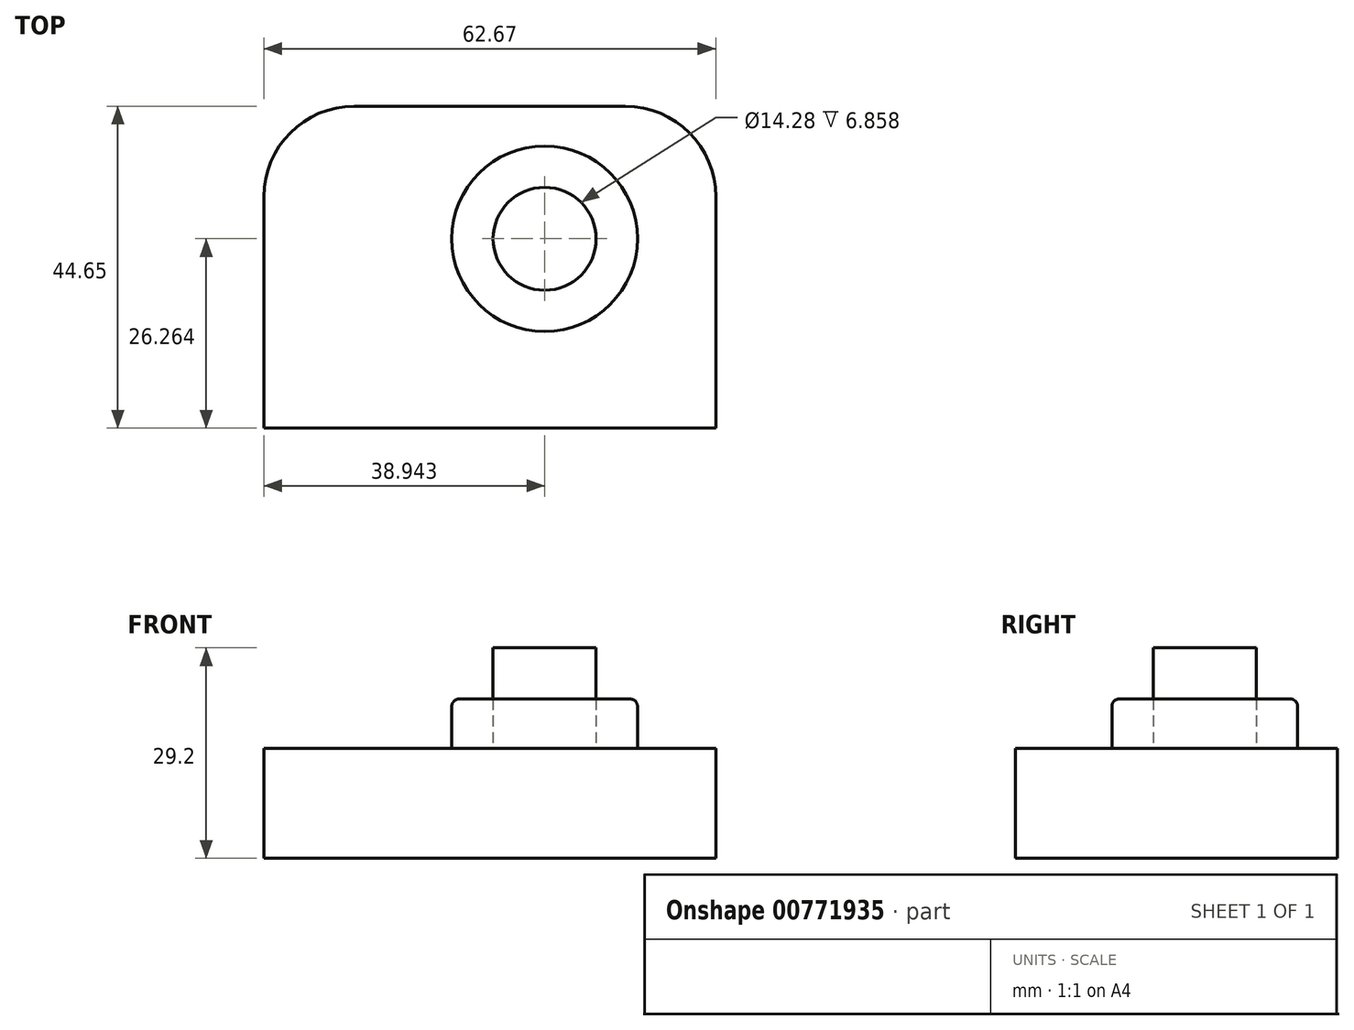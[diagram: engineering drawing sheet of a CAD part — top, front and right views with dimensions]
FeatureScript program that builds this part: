
annotation { "Feature Type Name" : "Feature", "Feature Type Description" : "" }
export const myFeature = defineFeature(function(context is Context, id is Id, definition is map)
    precondition{}
    {
        {
            var Q0;
            Q0=qCreatedBy(makeId("Top.planeOp"),FACE);
            var sketch = newSketch(context, id + "F0", { "sketchPlane" : qUnion([Q0])});
            skLineSegment(sketch, "E0.bottom", {"start": v(-68.94, 0) * mm, "end": v(-6.27, 0) * mm});
            skLineSegment(sketch, "E0.top", {"start": v(-68.94, -44.65) * mm, "end": v(-6.27, -44.65) * mm});
            skLineSegment(sketch, "E0.left", {"start": v(-68.94, 0) * mm, "end": v(-68.94, -44.65) * mm});
            skLineSegment(sketch, "E0.right", {"start": v(-6.27, 0) * mm, "end": v(-6.27, -44.65) * mm});
            skSolve(sketch);
        }
        {
            var Q0;
            Q0=qCreatedBy(makeId("Top.planeOp"),FACE);
            var sketch = newSketch(context, id + "F1", { "sketchPlane" : qUnion([Q0])});
            skSolve(sketch);
        }
        {
            var Q0;
            Q0 = qSketchRegion(id + "F1", true);
            var Q1;
            Q1=makeQuery(id+"F0.imprint","IMPRINT",FACE,{"disambiguationData":[TD([[makeQuery(id+"F0.imprint","IMPRINT",EDGE,{"derivedFrom":sQuery(id+"F0.wireOp",EDGE,"E0.bottom")}),-1.0]])]});
            extrude(context, id + "F2", {"entities" : qUnion([Q0, Q1]), "depth" : 15.24 * mm, "offsetDistance" : 25.4 * mm});
        }
        {
            var Q0;
            Q0=qCreatedBy(makeId("Top.planeOp"),FACE);
            var sketch = newSketch(context, id + "F3", { "sketchPlane" : qUnion([Q0])});
            skCircle(sketch, "E1", {"center": v(-26.07, -21.7) * mm, "radius": 8.82 * mm});
            skSolve(sketch);
        }
        {
            var Q0;
            Q0=makeQuery(id+"F2.opExtrude","CAP_FACE",FACE,{"disambiguationData":[OSD([sQuery(id+"F0.wireOp",EDGE,"E0.bottom"),sQuery(id+"F0.wireOp",EDGE,"E0.top"),sQuery(id+"F0.wireOp",EDGE,"E0.left"),sQuery(id+"F0.wireOp",EDGE,"E0.right")])],"isStart":false});
            var sketch = newSketch(context, id + "F4", { "sketchPlane" : qUnion([Q0])});
            skCircle(sketch, "E2", {"center": v(-30, -18.39) * mm, "radius": 12.87 * mm});
            skCircle(sketch, "E3", {"center": v(-30, -18.39) * mm, "radius": 7.14 * mm});
            skSolve(sketch);
        }
        {
            var Q0;
            Q0=makeQuery(id+"F4.imprint","IMPRINT",FACE,{"disambiguationData":[TD([[makeQuery(id+"F4.imprint","IMPRINT",EDGE,{"derivedFrom":sQuery(id+"F4.wireOp",EDGE,"E2")}),1.0]])]});
            var sketch = newSketch(context, id + "F5", { "sketchPlane" : qUnion([Q0])});
            skSolve(sketch);
        }
        {
            var Q0;
            Q0=makeQuery(id+"F5.imprint","IMPRINT",FACE,{"disambiguationData":[TD([[makeQuery(id+"F5.imprint","IMPRINT",EDGE,{"derivedFrom":makeQuery(id+"F4.imprint","IMPRINT",EDGE,{"derivedFrom":sQuery(id+"F4.wireOp",EDGE,"E2")})}),1.0]])]});
            extrude(context, id + "F6", {"entities" : qUnion([Q0]), "operationType" : NewBodyOperationType.ADD, "depth" : 6.86 * mm, "offsetDistance" : 25.4 * mm});
        }
        {
            var Q0;
            Q0=makeQuery(id+"F6.opExtrude","CAP_EDGE",EDGE,{"disambiguationData":[OSD([sQuery(id+"F4.wireOp",EDGE,"E2")])],"isStart":false});
            fillet(context, id + "F7", {"entities" : qUnion([Q0]), "radius" : 1 * mm, "tangentPropagation" : true, "allowEdgeOverflow" : false});
        }
        {
            var Q0;
            Q0=makeQuery(id+"F6.opExtrude","CAP_FACE",FACE,{"disambiguationData":[OSD([sQuery(id+"F4.wireOp",EDGE,"E2"),sQuery(id+"F4.wireOp",EDGE,"E3")])],"isStart":false});
            var sketch = newSketch(context, id + "F8", { "sketchPlane" : qUnion([Q0])});
            skSolve(sketch);
        }
        {
            var Q0;
            Q0=makeQuery(id+"F8.imprint","IMPRINT",FACE,{"disambiguationData":[TD([[makeQuery(id+"F8.imprint","IMPRINT",EDGE,{"derivedFrom":makeQuery(id+"F6.opExtrude","CAP_EDGE",EDGE,{"disambiguationData":[OSD([sQuery(id+"F4.wireOp",EDGE,"E3")])],"isStart":false})}),1.0]])]});
            extrude(context, id + "F9", {"entities" : qUnion([Q0]), "depth" : 7.1 * mm, "offsetDistance" : 25 * mm});
        }
        {
            var Q0;
            Q0=makeQuery(id+"F2.opExtrude","SWEPT_EDGE",EDGE,{"disambiguationData":[OSD([sQuery(id+"F0.wireOp",EDGE,"E0.bottom"),sQuery(id+"F0.wireOp",EDGE,"E0.left")])]});
            var Q1;
            Q1=makeQuery(id+"F2.opExtrude","SWEPT_EDGE",EDGE,{"disambiguationData":[OSD([sQuery(id+"F0.wireOp",EDGE,"E0.bottom"),sQuery(id+"F0.wireOp",EDGE,"E0.right")])]});
            fillet(context, id + "F10", {"entities" : qUnion([Q0, Q1]), "radius" : 12.55 * mm, "tangentPropagation" : true, "allowEdgeOverflow" : false});
        }
    });
